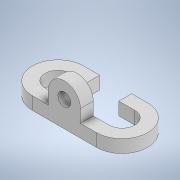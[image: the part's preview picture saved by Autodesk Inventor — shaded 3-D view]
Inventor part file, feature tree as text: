
AUTODESK INVENTOR PART (.ipt)
format: ipt  version: 2022.2 (Build 262287030, 287C)  size: 142,336 bytes
history: native  units: in
note: dims shown in document units (in); Inventor stores cm internally (conversion verified against a paired STEP export)
features: extrude x2, sketch x2, projected_geometry x1
ambient origin geometry x8: Origin, YZ Plane, XZ Plane, XY Plane, X Axis, Y Axis, Z Axis, Center Point
bodies: Solid1 (feature_tree)
feature tree (5):
  extrude  "Extrusion1"  Depth=1.0in
  extrude  "Extrusion2"  Depth=0.5in TaperAngle=0.0deg
  sketch  "Sketch2"  dims[d0=0.625in d1=1.0in]
  sketch  "Sketch3"  dims[d2=0.5in d4=0.5in d5=0.0in d6=2.5in d7=0.5in d9=1.25in d10=0.5in d11=0.0in]
  projected_geometry  "Projected Loop1"
